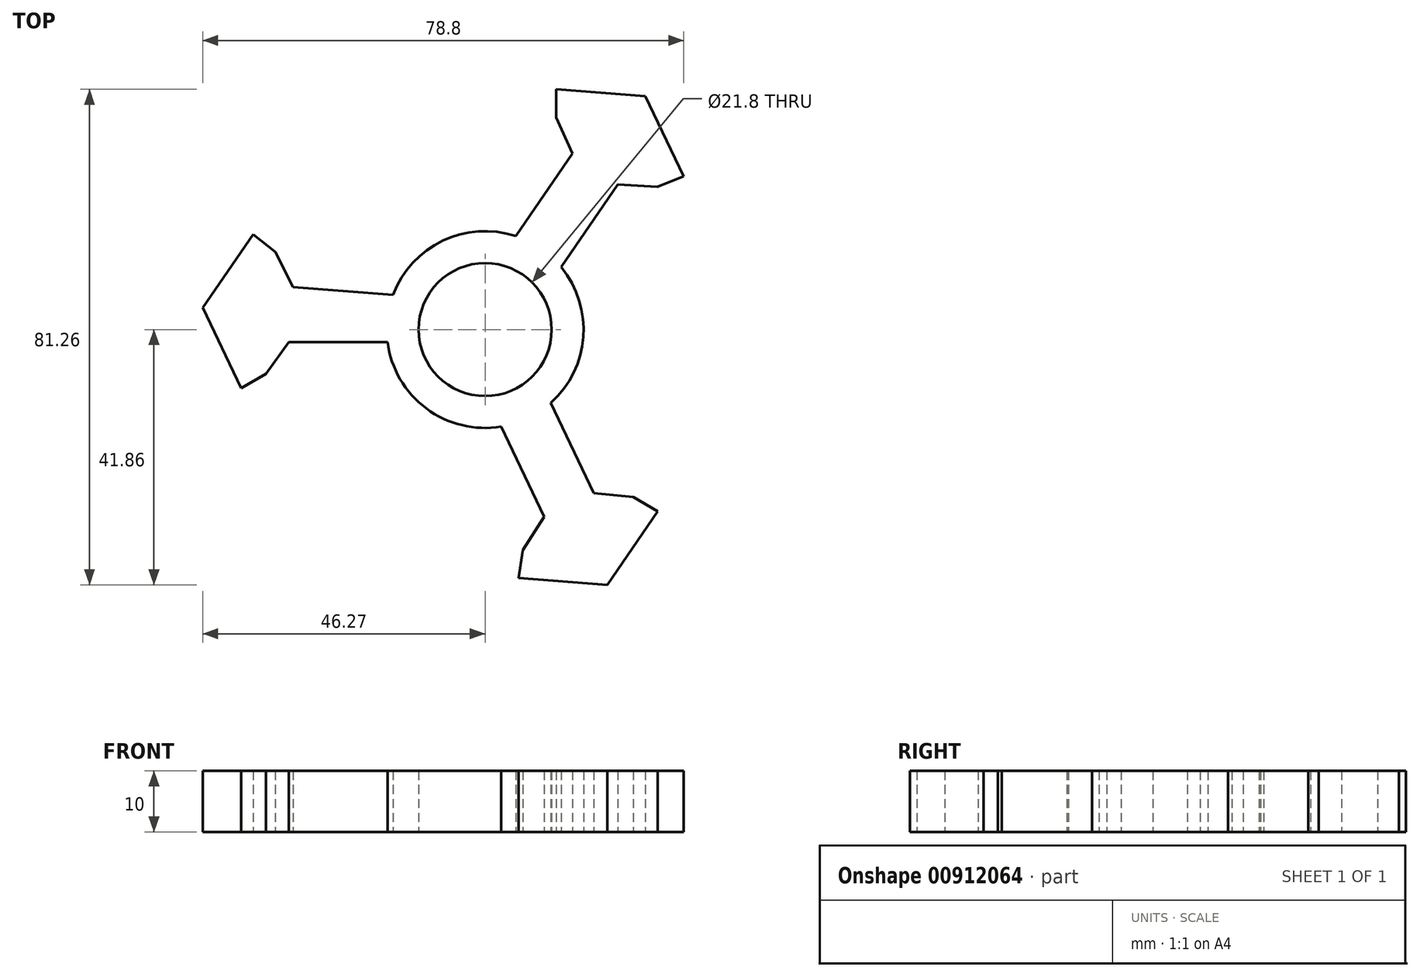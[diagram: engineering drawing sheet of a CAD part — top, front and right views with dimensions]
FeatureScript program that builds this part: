
annotation { "Feature Type Name" : "Feature", "Feature Type Description" : "" }
export const myFeature = defineFeature(function(context is Context, id is Id, definition is map)
    precondition{}
    {
        {
            var Q0;
            Q0=qCreatedBy(makeId("Top.planeOp"),FACE);
            var sketch = newSketch(context, id + "F0", { "sketchPlane" : qUnion([Q0])});
            skCircle(sketch, "E0", {"center": v(0, 0) * mm, "radius": 16.13 * mm});
            skLineSegment(sketch, "E1", {"start": v(0, 0) * mm, "end": v(26.23, 38.29) * mm});
            skLineSegment(sketch, "E2", {"start": v(0, 0) * mm, "end": v(20.04, -41.86) * mm});
            skLineSegment(sketch, "E3", {"start": v(0, 0) * mm, "end": v(-46.27, 3.57) * mm});
            skLineSegment(sketch, "E4", {"start": v(18.02, 26.3) * mm, "end": v(14.3, 28.85) * mm});
            skLineSegment(sketch, "E5", {"start": v(14.3, 28.85) * mm, "end": v(11.66, 34.76) * mm});
            skLineSegment(sketch, "E6", {"start": v(11.66, 34.76) * mm, "end": v(11.66, 39.4) * mm});
            skLineSegment(sketch, "E7", {"start": v(11.66, 39.4) * mm, "end": v(26.23, 38.29) * mm});
            skLineSegment(sketch, "E8.MirrorCS", {"start": v(32.53, 25.1) * mm, "end": v(26.23, 38.29) * mm});
            skLineSegment(sketch, "E9.MirrorCS", {"start": v(28.2, 23.43) * mm, "end": v(32.53, 25.1) * mm});
            skLineSegment(sketch, "E10.MirrorCS", {"start": v(21.74, 23.76) * mm, "end": v(28.2, 23.43) * mm});
            skLineSegment(sketch, "E11.MirrorCS", {"start": v(18.02, 26.3) * mm, "end": v(21.74, 23.76) * mm});
            skLineSegment(sketch, "E12.MirrorCS", {"start": v(-34.39, 12.71) * mm, "end": v(-38, 15.62) * mm});
            skLineSegment(sketch, "E13.MirrorCS", {"start": v(-31.8, 2.46) * mm, "end": v(-31.45, 6.95) * mm});
            skLineSegment(sketch, "E14.MirrorCS", {"start": v(-35.93, -7.28) * mm, "end": v(-39.95, -9.6) * mm});
            skLineSegment(sketch, "E15.MirrorCS", {"start": v(-31.8, 2.46) * mm, "end": v(-32.14, -2.04) * mm});
            skLineSegment(sketch, "E16.MirrorCS", {"start": v(-38, 15.62) * mm, "end": v(-46.27, 3.57) * mm});
            skLineSegment(sketch, "E17.MirrorCS", {"start": v(-31.45, 6.95) * mm, "end": v(-34.39, 12.71) * mm});
            skLineSegment(sketch, "E18.MirrorCS", {"start": v(-39.95, -9.6) * mm, "end": v(-46.27, 3.57) * mm});
            skLineSegment(sketch, "E19.MirrorCS", {"start": v(-32.14, -2.04) * mm, "end": v(-35.93, -7.28) * mm});
            skLineSegment(sketch, "E20.MirrorCS", {"start": v(6.18, -36.14) * mm, "end": v(5.47, -40.72) * mm});
            skLineSegment(sketch, "E21.MirrorCS", {"start": v(13.77, -28.76) * mm, "end": v(17.83, -26.82) * mm});
            skLineSegment(sketch, "E22.MirrorCS", {"start": v(24.27, -27.48) * mm, "end": v(28.29, -29.8) * mm});
            skLineSegment(sketch, "E23.MirrorCS", {"start": v(13.77, -28.76) * mm, "end": v(9.7, -30.7) * mm});
            skLineSegment(sketch, "E24.MirrorCS", {"start": v(28.29, -29.8) * mm, "end": v(20.04, -41.86) * mm});
            skLineSegment(sketch, "E25.MirrorCS", {"start": v(17.83, -26.82) * mm, "end": v(24.27, -27.48) * mm});
            skLineSegment(sketch, "E26.MirrorCS", {"start": v(9.7, -30.7) * mm, "end": v(6.18, -36.14) * mm});
            skLineSegment(sketch, "E27.MirrorCS", {"start": v(5.47, -40.72) * mm, "end": v(20.04, -41.86) * mm});
            skLineSegment(sketch, "E28", {"start": v(-31.45, 6.95) * mm, "end": v(-15.1, 5.68) * mm});
            skLineSegment(sketch, "E29", {"start": v(-32.14, -2.04) * mm, "end": v(-16, -2.04) * mm});
            skLineSegment(sketch, "E30", {"start": v(21.74, 23.76) * mm, "end": v(12.47, 10.23) * mm});
            skLineSegment(sketch, "E31", {"start": v(14.3, 28.85) * mm, "end": v(5.04, 15.33) * mm});
            skLineSegment(sketch, "E32", {"start": v(17.83, -26.82) * mm, "end": v(10.75, -12.03) * mm});
            skLineSegment(sketch, "E33", {"start": v(9.7, -30.7) * mm, "end": v(2.63, -15.92) * mm});
            skCircle(sketch, "E34", {"center": v(0, 0) * mm, "radius": 10.9 * mm});
            skSolve(sketch);
        }
        {
            var Q0;
            Q0 = qSketchRegion(id + "F0", true);
            extrude(context, id + "F1", {"entities" : qUnion([Q0]), "depth" : 10 * mm, "offsetDistance" : 25 * mm});
        }
    });
